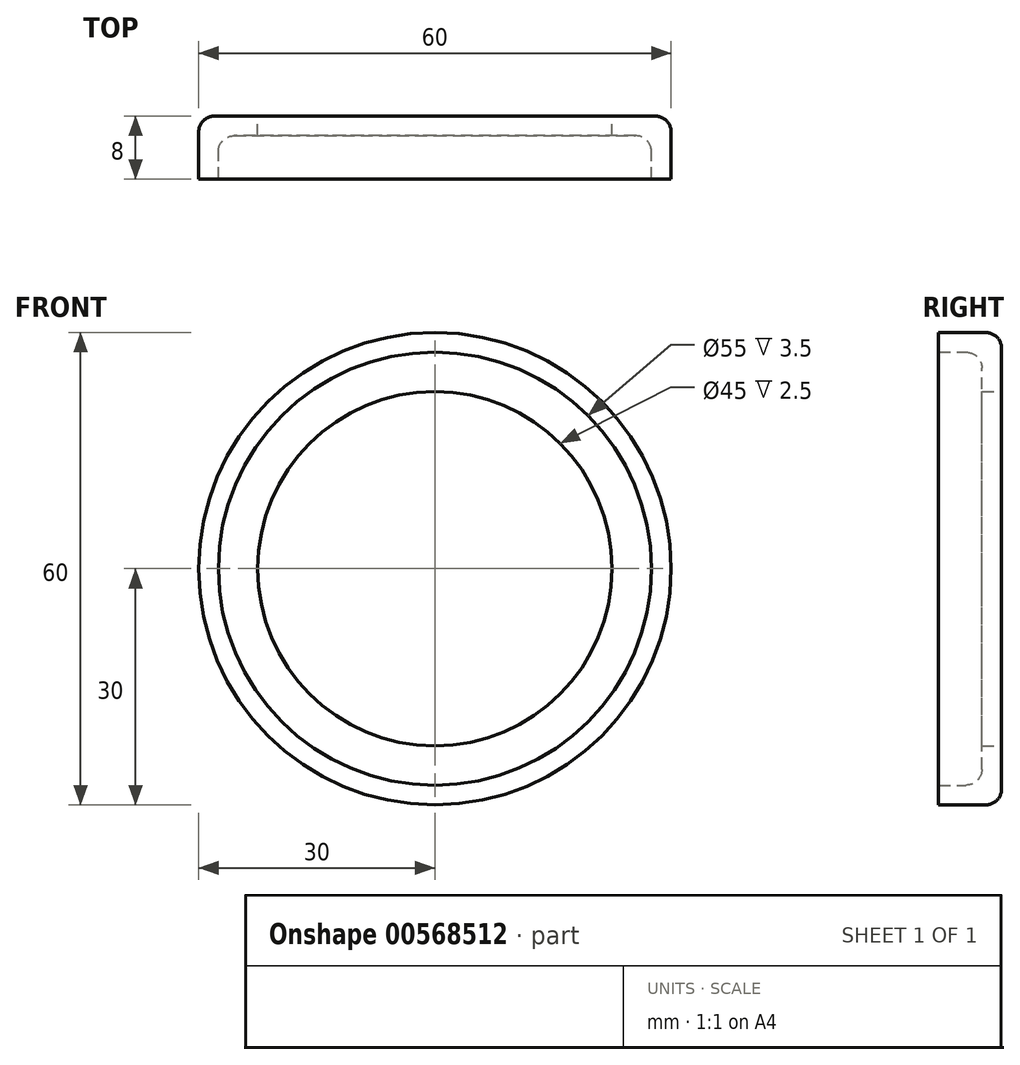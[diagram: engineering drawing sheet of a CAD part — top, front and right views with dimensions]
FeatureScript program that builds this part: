
annotation { "Feature Type Name" : "Feature", "Feature Type Description" : "" }
export const myFeature = defineFeature(function(context is Context, id is Id, definition is map)
    precondition{}
    {
        {
            var Q0;
            Q0=qCreatedBy(makeId("Front.planeOp"),FACE);
            var sketch = newSketch(context, id + "F0", { "sketchPlane" : qUnion([Q0])});
            skCircle(sketch, "E0", {"center": v(0, 0) * mm, "radius": 30 * mm});
            skSolve(sketch);
        }
        {
            var Q0;
            Q0=makeQuery(id+"F0.imprint","IMPRINT",FACE,{"disambiguationData":[TD([[makeQuery(id+"F0.imprint","IMPRINT",EDGE,{"derivedFrom":sQuery(id+"F0.wireOp",EDGE,"E0")}),1.0]])]});
            extrude(context, id + "F1", {"entities" : qUnion([Q0]), "depth" : 8 * mm, "offsetDistance" : 25 * mm});
        }
        {
            var Q0;
            Q0=makeQuery(id+"F1.opExtrude","CAP_FACE",FACE,{"disambiguationData":[OSD([sQuery(id+"F0.wireOp",EDGE,"E0")])],"isStart":false});
            shell(context, id + "F2", {"entities" : qUnion([Q0]), "thickness" : 2.5 * mm});
        }
        {
            var Q0;
            Q0=makeQuery(id+"F1.opExtrude","CAP_FACE",FACE,{"disambiguationData":[OSD([sQuery(id+"F0.wireOp",EDGE,"E0")])],"isStart":true});
            var sketch = newSketch(context, id + "F3", { "sketchPlane" : qUnion([Q0])});
            skCircle(sketch, "E1", {"center": v(0, 0) * mm, "radius": 22.5 * mm});
            skSolve(sketch);
        }
        {
            var Q0;
            Q0=makeQuery(id+"F3.imprint","IMPRINT",FACE,{"disambiguationData":[TD([[makeQuery(id+"F3.imprint","IMPRINT",EDGE,{"derivedFrom":sQuery(id+"F3.wireOp",EDGE,"E1")}),1.0]])]});
            extrude(context, id + "F4", {"entities" : qUnion([Q0]), "operationType" : NewBodyOperationType.REMOVE, "oppositeDirection" : true, "depth" : 25 * mm, "offsetDistance" : 25 * mm});
        }
        {
            var Q0;
            Q0=makeQuery(id+"F1.opExtrude","CAP_EDGE",EDGE,{"disambiguationData":[OSD([sQuery(id+"F0.wireOp",EDGE,"E0")])],"isStart":true});
            fillet(context, id + "F5", {"entities" : qUnion([Q0]), "radius" : 2 * mm, "tangentPropagation" : true, "allowEdgeOverflow" : false});
        }
        {
            var Q0;
            {var subQ0=sQuery(id+"F0.wireOp",EDGE,"E0");Q0=makeQuery(id+"F2.opShell","OFFSET_EDGE",EDGE,{"disambiguationData":[OSD([subQ0]),TDD([makeQuery(id+"F1.opExtrude","CAP_EDGE",EDGE,{"disambiguationData":[OSD([subQ0])],"isStart":true})])]});}
            fillet(context, id + "F6", {"entities" : qUnion([Q0]), "radius" : 2 * mm, "tangentPropagation" : true, "allowEdgeOverflow" : false});
        }
    });
